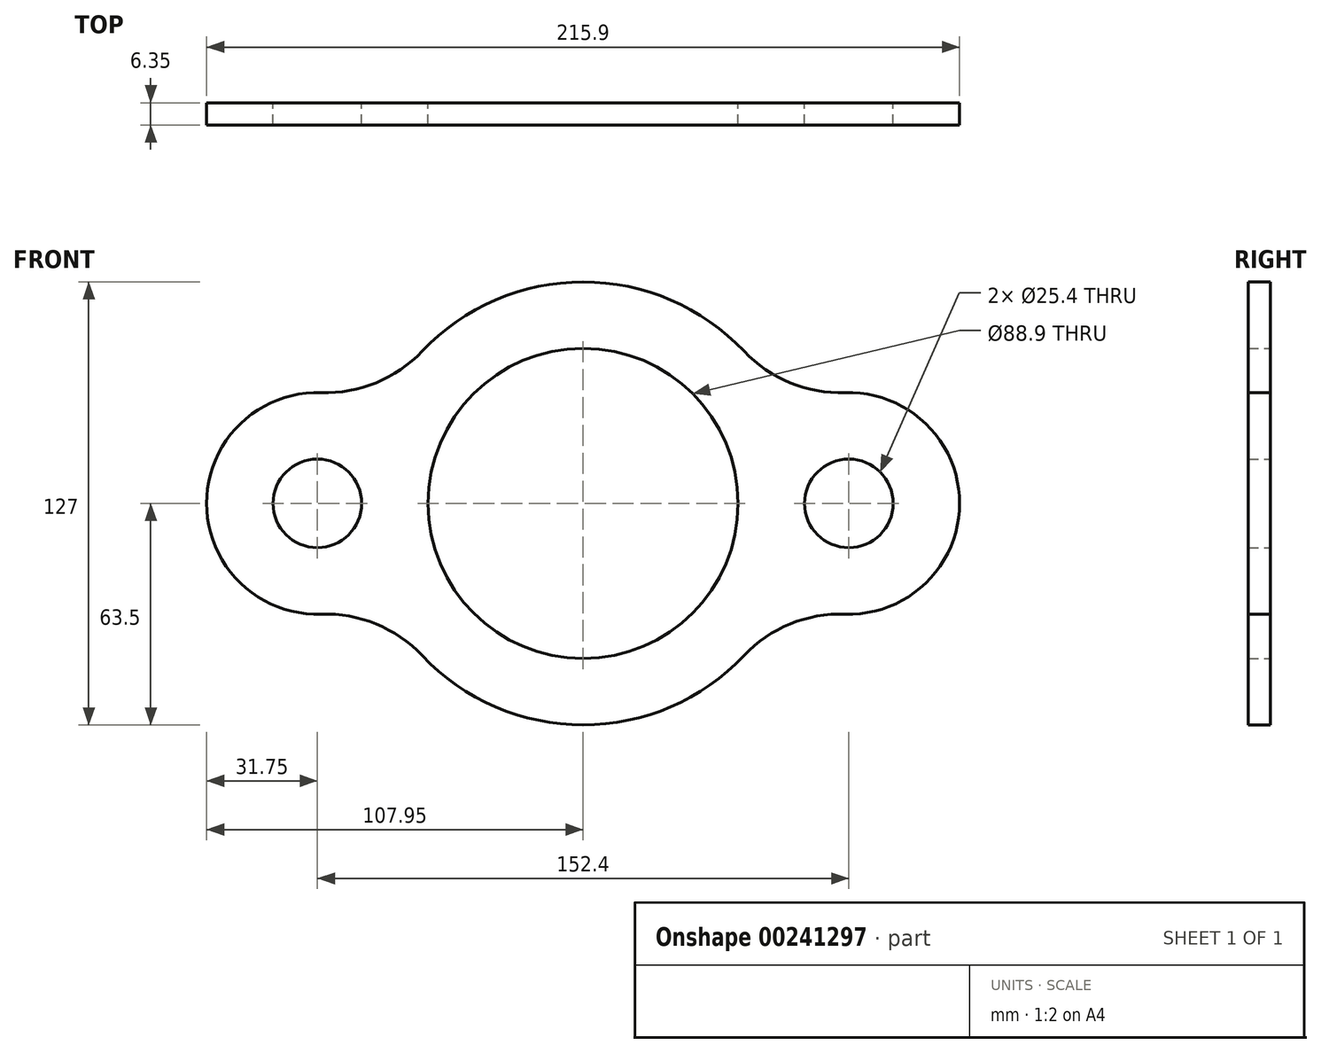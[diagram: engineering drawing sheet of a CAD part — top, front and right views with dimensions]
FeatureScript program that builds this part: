
annotation { "Feature Type Name" : "Feature", "Feature Type Description" : "" }
export const myFeature = defineFeature(function(context is Context, id is Id, definition is map)
    precondition{}
    {
        {
            var Q0;
            Q0=qCreatedBy(makeId("Front.planeOp"),FACE);
            var sketch = newSketch(context, id + "F0", { "sketchPlane" : qUnion([Q0])});
            skArc(sketch, "E0", {"start": v(-46.14, -43.63) * mm, "mid": v(0, -63.5) * mm, "end": v(46.14, -43.63) * mm});
            skLineSegment(sketch, "E1", {"start": v(0, 0) * mm, "end": v(-44.45, 0) * mm});
            skLineSegment(sketch, "E2", {"start": v(0, 0) * mm, "end": v(44.45, 0) * mm});
            skCircle(sketch, "E3", {"center": v(-76.2, 0) * mm, "radius": 12.7 * mm});
            skCircle(sketch, "E4", {"center": v(76.2, 0) * mm, "radius": 12.7 * mm});
            skCircle(sketch, "E5", {"center": v(0, 0) * mm, "radius": 44.45 * mm});
            skArc(sketch, "E6", {"start": v(-75.12, 31.73) * mm, "mid": v(-107.95, 0) * mm, "end": v(-75.12, -31.73) * mm});
            skArc(sketch, "E7", {"start": v(75.12, -31.73) * mm, "mid": v(107.95, 0) * mm, "end": v(75.12, 31.73) * mm});
            skArc(sketch, "E8.trimOffspring", {"start": v(46.14, 43.63) * mm, "mid": v(0, 63.5) * mm, "end": v(-46.14, 43.63) * mm});
            skArc(sketch, "E9", {"start": v(-75.12, 31.73) * mm, "mid": v(-59.35, 34.56) * mm, "end": v(-46.14, 43.63) * mm});
            skArc(sketch, "E10", {"start": v(46.14, 43.63) * mm, "mid": v(59.35, 34.56) * mm, "end": v(75.12, 31.73) * mm});
            skArc(sketch, "E11", {"start": v(75.12, -31.73) * mm, "mid": v(59.35, -34.56) * mm, "end": v(46.14, -43.63) * mm});
            skArc(sketch, "E12", {"start": v(-46.14, -43.63) * mm, "mid": v(-59.35, -34.56) * mm, "end": v(-75.12, -31.73) * mm});
            skSolve(sketch);
        }
        {
            var Q0;
            Q0=makeQuery(id+"F0.imprint","IMPRINT",FACE,{"disambiguationData":[TD([[makeQuery(id+"F0.imprint","IMPRINT",EDGE,{"derivedFrom":sQuery(id+"F0.wireOp",EDGE,"E0")}),1.0]])]});
            extrude(context, id + "F1", {"entities" : qUnion([Q0]), "depth" : 6.35 * mm});
        }
    });
